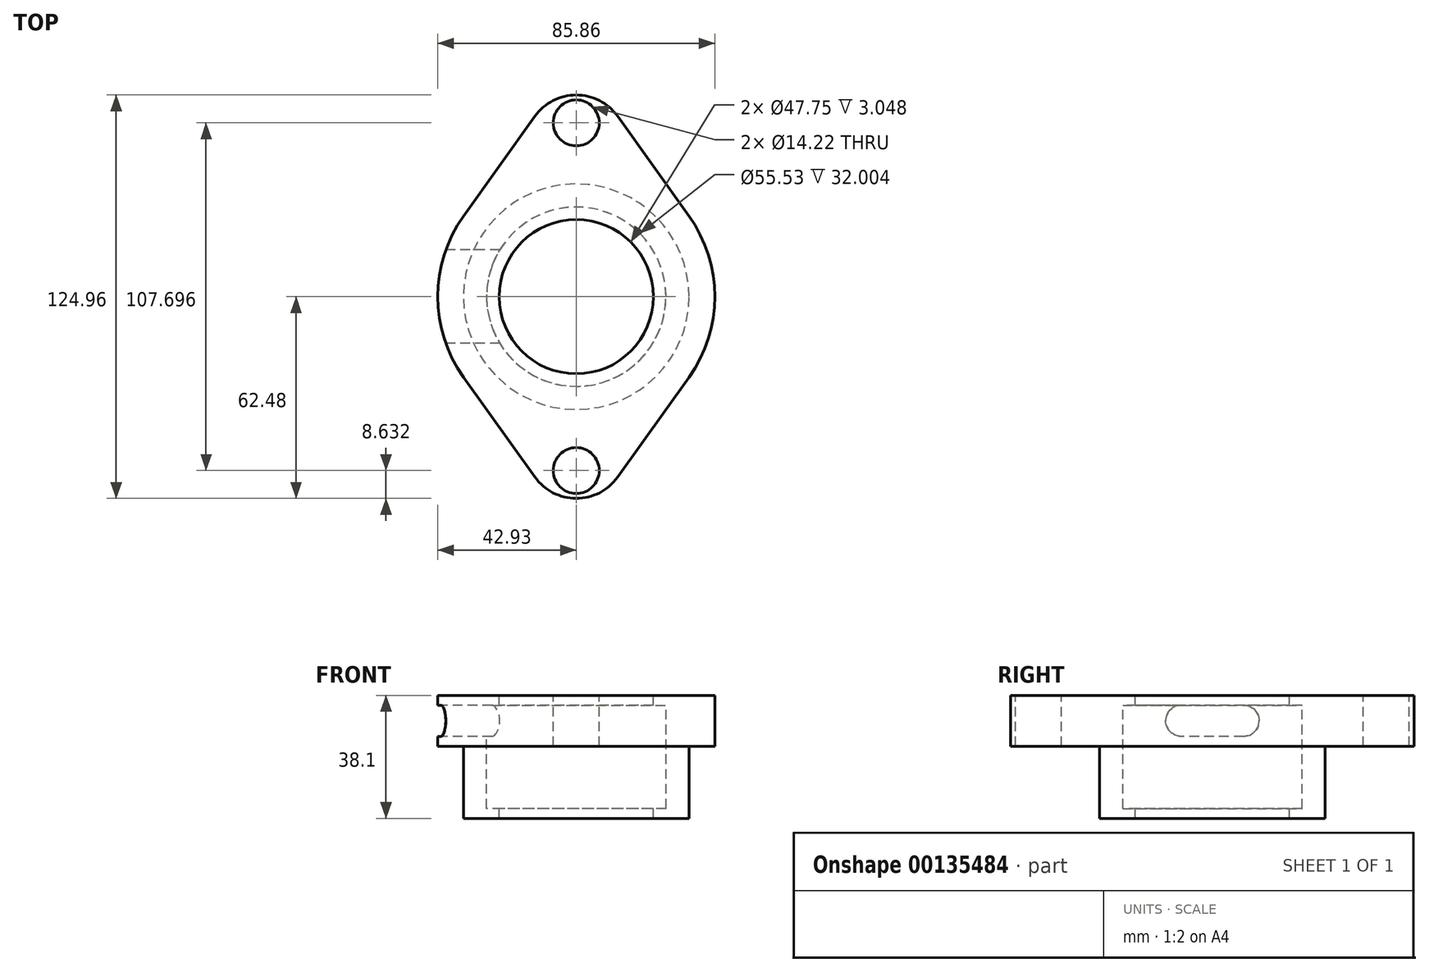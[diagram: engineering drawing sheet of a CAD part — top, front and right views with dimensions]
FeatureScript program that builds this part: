
annotation { "Feature Type Name" : "Feature", "Feature Type Description" : "" }
export const myFeature = defineFeature(function(context is Context, id is Id, definition is map)
    precondition{}
    {
        {
            var Q0;
            Q0=qCreatedBy(makeId("Top.planeOp"),FACE);
            var sketch = newSketch(context, id + "F0", { "sketchPlane" : qUnion([Q0])});
            skCircle(sketch, "E0", {"center": v(0, 0) * mm, "radius": 23.88 * mm});
            skCircle(sketch, "E1", {"center": v(0, 0) * mm, "radius": 34.93 * mm});
            skLineSegment(sketch, "E2", {"start": v(-12.81, 55.9) * mm, "end": v(-34.92, 24.96) * mm});
            skLineSegment(sketch, "E3", {"start": v(12.81, 55.9) * mm, "end": v(34.92, 24.96) * mm});
            skArc(sketch, "E4", {"start": v(12.81, 55.9) * mm, "mid": v(0, 62.48) * mm, "end": v(-12.81, 55.9) * mm});
            skPoint(sketch, "E5", {"position": v(0, 62.48) * mm});
            skLineSegment(sketch, "E6", {"start": v(0, 0) * mm, "end": v(0, 41.17) * mm, "construction": true});
            skLineSegment(sketch, "E7", {"start": v(-32.08, 55.9) * mm, "end": v(22.25, 55.9) * mm, "construction": true});
            skLineSegment(sketch, "E8", {"start": v(-27.77, 0) * mm, "end": v(29.34, 0) * mm, "construction": true});
            skLineSegment(sketch, "E9.MirrorCS", {"start": v(12.81, -55.9) * mm, "end": v(34.92, -24.96) * mm});
            skArc(sketch, "E10.MirrorCS", {"start": v(12.81, -55.9) * mm, "mid": v(0, -62.48) * mm, "end": v(-12.81, -55.9) * mm});
            skLineSegment(sketch, "E11.MirrorCS", {"start": v(-12.81, -55.9) * mm, "end": v(-34.92, -24.96) * mm});
            skLineSegment(sketch, "E12.MirrorCS", {"start": v(0, 0) * mm, "end": v(0, -41.17) * mm, "construction": true});
            skLineSegment(sketch, "E13.MirrorCS", {"start": v(-32.08, -55.9) * mm, "end": v(22.25, -55.9) * mm, "construction": true});
            skArc(sketch, "E14", {"start": v(-34.92, 24.96) * mm, "mid": v(-42.93, 0) * mm, "end": v(-34.92, -24.96) * mm});
            skArc(sketch, "E15", {"start": v(34.92, -24.96) * mm, "mid": v(42.93, 0) * mm, "end": v(34.92, 24.96) * mm});
            skCircle(sketch, "E16", {"center": v(0, 53.85) * mm, "radius": 7.11 * mm});
            skCircle(sketch, "E17.MirrorC", {"center": v(0, -53.85) * mm, "radius": 7.11 * mm});
            skSolve(sketch);
        }
        {
            var Q0;
            Q0=makeQuery(id+"F0.imprint","IMPRINT",FACE,{"disambiguationData":[TD([[makeQuery(id+"F0.imprint","IMPRINT",EDGE,{"derivedFrom":sQuery(id+"F0.wireOp",EDGE,"E0")}),-1.0]])]});
            extrude(context, id + "F1", {"entities" : qUnion([Q0]), "oppositeDirection" : true, "depth" : 38.1 * mm});
        }
        {
            var Q0;
            Q0=makeQuery(id+"F0.imprint","IMPRINT",FACE,{"disambiguationData":[TD([[makeQuery(id+"F0.imprint","IMPRINT",EDGE,{"derivedFrom":sQuery(id+"F0.wireOp",EDGE,"E0")}),-1.0]])]});
            var sketch = newSketch(context, id + "F2", { "sketchPlane" : qUnion([Q0])});
            skCircle(sketch, "E18", {"center": v(0, 0) * mm, "radius": 27.77 * mm});
            skCircle(sketch, "E19", {"center": v(0, 0) * mm, "radius": 23.88 * mm});
            skCircle(sketch, "E20", {"center": v(0, 0) * mm, "radius": 34.93 * mm});
            skSolve(sketch);
        }
        {
            var Q0;
            Q0=makeQuery(id+"F2.imprint","IMPRINT",FACE,{"disambiguationData":[TD([[makeQuery(id+"F2.imprint","IMPRINT",EDGE,{"derivedFrom":sQuery(id+"F2.wireOp",EDGE,"E18")}),1.0]])]});
            var Q1;
            Q1=sQuery(id+"F2.wireOp",EDGE,"E18");
            extrude(context, id + "F3", {"entities" : qUnion([Q0]), "operationType" : NewBodyOperationType.REMOVE, "surfaceEntities" : qUnion([Q1]), "oppositeDirection" : true, "depth" : 35.05 * mm, "hasSecondDirection" : true, "secondDirectionOppositeDirection" : true, "secondDirectionDepth" : 3.05 * mm});
        }
        {
            var Q0;
            Q0=makeQuery(id+"F0.imprint","IMPRINT",FACE,{"disambiguationData":[TD([[makeQuery(id+"F0.imprint","IMPRINT",EDGE,{"derivedFrom":sQuery(id+"F0.wireOp",EDGE,"E1")}),-1.0]])]});
            extrude(context, id + "F4", {"entities" : qUnion([Q0]), "operationType" : NewBodyOperationType.ADD, "oppositeDirection" : true, "depth" : 15.75 * mm});
        }
        {
            var Q0;
            Q0=qCreatedBy(makeId("Right.planeOp"),FACE);
            cPlane(context, id + "F5", {"entities" : qUnion([Q0]), "cplaneType" : CPlaneType.OFFSET, "offset" : 50.8 * mm, "oppositeDirection" : true, "width" : 152.4 * mm, "height" : 152.4 * mm});
        }
        {
            var Q0;
            Q0=qCreatedBy(id+"F5.planeOp",FACE);
            var sketch = newSketch(context, id + "F6", { "sketchPlane" : qUnion([Q0])});
            skLineSegment(sketch, "E21.bottom", {"start": v(-24.96, 0) * mm, "end": v(24.96, 0) * mm});
            skLineSegment(sketch, "E21.top", {"start": v(-24.96, -15.75) * mm, "end": v(24.96, -15.75) * mm});
            skLineSegment(sketch, "E21.left", {"start": v(-24.96, 0) * mm, "end": v(-24.96, -15.75) * mm});
            skLineSegment(sketch, "E21.right", {"start": v(24.96, 0) * mm, "end": v(24.96, -15.75) * mm});
            skLineSegment(sketch, "E22.bottom", {"start": v(-9.65, -3.05) * mm, "end": v(9.65, -3.05) * mm});
            skLineSegment(sketch, "E22.top", {"start": v(-9.65, -12.7) * mm, "end": v(9.65, -12.7) * mm});
            skArc(sketch, "E23", {"start": v(-9.65, -3.05) * mm, "mid": v(-14.48, -7.87) * mm, "end": v(-9.65, -12.7) * mm});
            skArc(sketch, "E24", {"start": v(9.65, -12.7) * mm, "mid": v(14.48, -7.87) * mm, "end": v(9.65, -3.05) * mm});
            skLineSegment(sketch, "E25", {"start": v(-24.96, -7.87) * mm, "end": v(-9.65, -7.87) * mm, "construction": true});
            skLineSegment(sketch, "E26.trimOffspring", {"start": v(9.65, -7.87) * mm, "end": v(24.96, -7.87) * mm, "construction": true});
            skSolve(sketch);
        }
        {
            var Q0;
            Q0=makeQuery(id+"F6.imprint","IMPRINT",FACE,{"disambiguationData":[TD([[makeQuery(id+"F6.imprint","IMPRINT",EDGE,{"derivedFrom":sQuery(id+"F6.wireOp",EDGE,"E22.bottom")}),-1.0]])]});
            var Q1;
            Q1=makeQuery(id+"F3.boolean.opBoolean","COPY",FACE,{"derivedFrom":makeQuery(id+"F3.opExtrude","SWEPT_FACE",FACE,{"disambiguationData":[OSD([sQuery(id+"F2.wireOp",EDGE,"E18")])]})});
            extrude(context, id + "F7", {"entities" : qUnion([Q0]), "operationType" : NewBodyOperationType.REMOVE, "endBound" : BoundingType.UP_TO_SURFACE, "endBoundEntityFace" : qUnion([Q1]), "depth" : 25.4 * mm});
        }
    });
